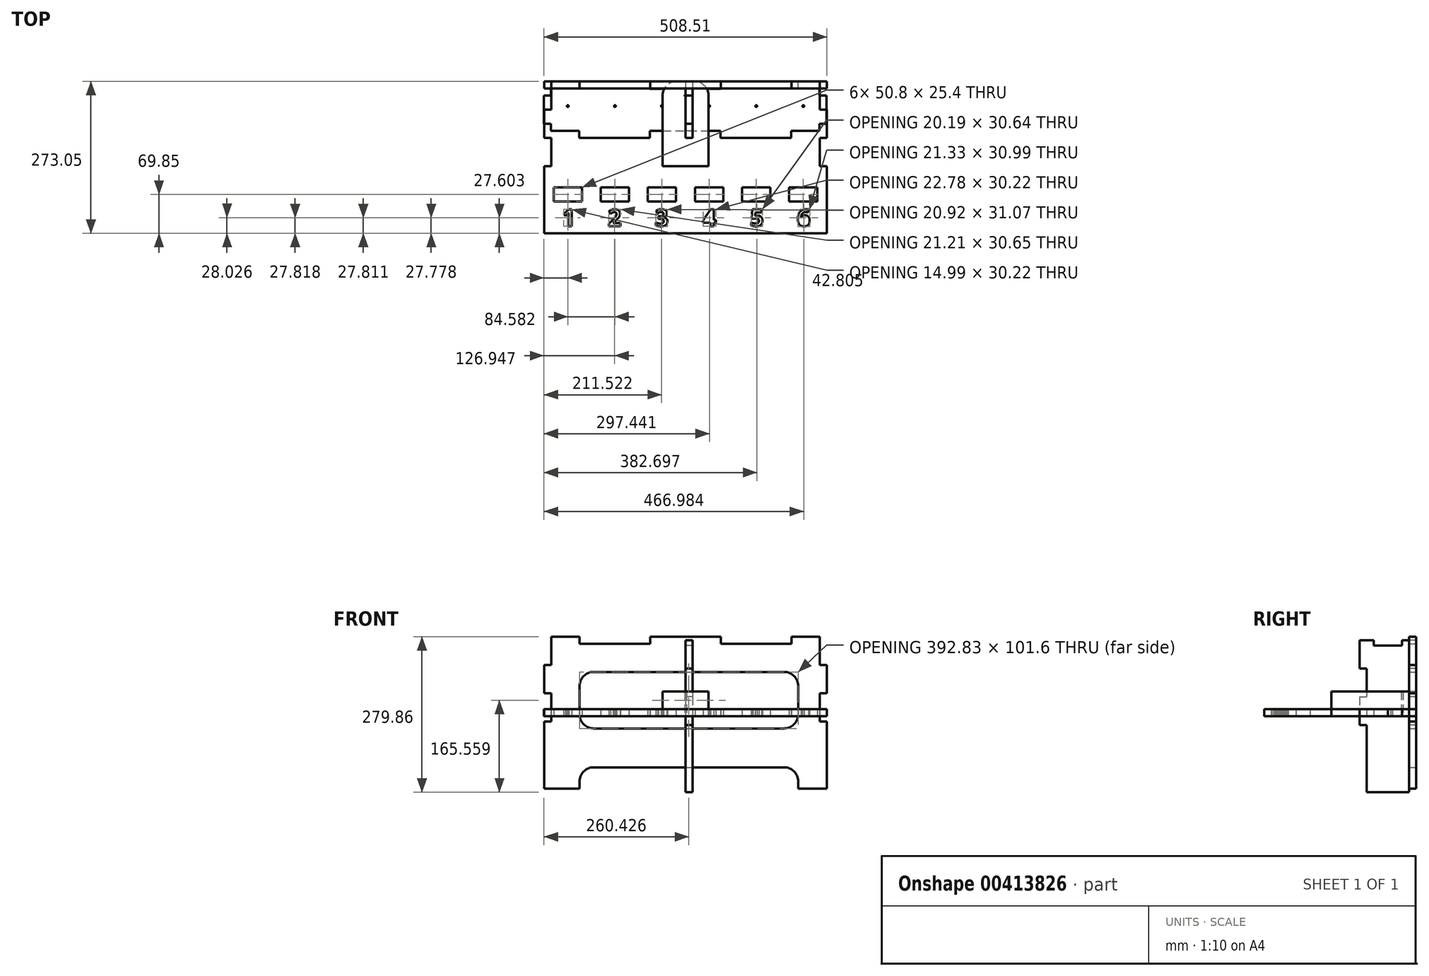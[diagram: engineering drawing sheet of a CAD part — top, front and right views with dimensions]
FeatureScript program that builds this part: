
annotation { "Feature Type Name" : "Feature", "Feature Type Description" : "" }
export const myFeature = defineFeature(function(context is Context, id is Id, definition is map)
    precondition{}
    {
        {
            var Q0;
            Q0=qCreatedBy(makeId("Top.planeOp"),FACE);
            var sketch = newSketch(context, id + "F0", { "sketchPlane" : qUnion([Q0])});
            skLineSegment(sketch, "E0.bottom", {"start": v(-15.88, 0) * mm, "end": v(15.88, 0) * mm});
            skLineSegment(sketch, "E0.top", {"start": v(-41.28, -152.4) * mm, "end": v(41.28, -152.4) * mm});
            skLineSegment(sketch, "E0.left", {"start": v(-41.28, -25.4) * mm, "end": v(-41.28, -152.4) * mm});
            skLineSegment(sketch, "E0.right", {"start": v(41.28, -25.4) * mm, "end": v(41.28, -152.4) * mm});
            skPoint(sketch, "E1.visualSharp", {"position": v(-41.28, 0) * mm});
            skArc(sketch, "E1.filletArc", {"start": v(-15.88, 0) * mm, "mid": v(-33.84, -7.44) * mm, "end": v(-41.28, -25.4) * mm});
            skPoint(sketch, "E2.visualSharp", {"position": v(41.28, 0) * mm});
            skArc(sketch, "E2.filletArc", {"start": v(41.28, -25.4) * mm, "mid": v(33.84, -7.44) * mm, "end": v(15.88, 0) * mm});
            skCircle(sketch, "E3", {"center": v(0, -25.4) * mm, "radius": 1.59 * mm});
            skSolve(sketch);
        }
        {
            var Q0;
            Q0 = qSketchRegion(id + "F0", true);
            extrude(context, id + "F1", {"entities" : qUnion([Q0]), "depth" : 44.45 * mm});
        }
        {
            var Q0;
            Q0=qCreatedBy(makeId("Top.planeOp"),FACE);
            var sketch = newSketch(context, id + "F2", { "sketchPlane" : qUnion([Q0])});
            skLineSegment(sketch, "E4.bottom", {"start": v(-241.3, 0) * mm, "end": v(-190.5, 0) * mm});
            skLineSegment(sketch, "E4.top", {"start": v(-254, -273.05) * mm, "end": v(254, -273.05) * mm});
            skLineSegment(sketch, "E4.left", {"start": v(-254, -50.8) * mm, "end": v(-254, -101.6) * mm});
            skLineSegment(sketch, "E4.right", {"start": v(254, -50.8) * mm, "end": v(254, -101.6) * mm});
            skLineSegment(sketch, "E5.bottom", {"start": v(-236.98, -190.5) * mm, "end": v(-186.18, -190.5) * mm});
            skLineSegment(sketch, "E5.top", {"start": v(-236.98, -215.9) * mm, "end": v(-186.18, -215.9) * mm});
            skLineSegment(sketch, "E5.left", {"start": v(-236.98, -190.5) * mm, "end": v(-236.98, -215.9) * mm});
            skLineSegment(sketch, "E5.right", {"start": v(-186.18, -190.5) * mm, "end": v(-186.18, -215.9) * mm});
            skLineSegment(sketch, "E6.bottom", {"start": v(-152.4, -190.5) * mm, "end": v(-101.6, -190.5) * mm});
            skLineSegment(sketch, "E6.top", {"start": v(-152.4, -215.9) * mm, "end": v(-101.6, -215.9) * mm});
            skLineSegment(sketch, "E6.left", {"start": v(-152.4, -190.5) * mm, "end": v(-152.4, -215.9) * mm});
            skLineSegment(sketch, "E6.right", {"start": v(-101.6, -190.5) * mm, "end": v(-101.6, -215.9) * mm});
            skLineSegment(sketch, "E7.bottom", {"start": v(-67.82, -190.5) * mm, "end": v(-17.02, -190.5) * mm});
            skLineSegment(sketch, "E7.top", {"start": v(-67.82, -215.9) * mm, "end": v(-17.02, -215.9) * mm});
            skLineSegment(sketch, "E7.left", {"start": v(-67.82, -190.5) * mm, "end": v(-67.82, -215.9) * mm});
            skLineSegment(sketch, "E7.right", {"start": v(-17.02, -190.5) * mm, "end": v(-17.02, -215.9) * mm});
            skLineSegment(sketch, "E8.bottom", {"start": v(236.98, -190.5) * mm, "end": v(186.18, -190.5) * mm});
            skLineSegment(sketch, "E8.top", {"start": v(236.98, -215.9) * mm, "end": v(186.18, -215.9) * mm});
            skLineSegment(sketch, "E8.left", {"start": v(236.98, -190.5) * mm, "end": v(236.98, -215.9) * mm});
            skLineSegment(sketch, "E8.right", {"start": v(186.18, -190.5) * mm, "end": v(186.18, -215.9) * mm});
            skLineSegment(sketch, "E9.bottom", {"start": v(152.4, -190.5) * mm, "end": v(101.6, -190.5) * mm});
            skLineSegment(sketch, "E9.top", {"start": v(152.4, -215.9) * mm, "end": v(101.6, -215.9) * mm});
            skLineSegment(sketch, "E9.left", {"start": v(152.4, -190.5) * mm, "end": v(152.4, -215.9) * mm});
            skLineSegment(sketch, "E9.right", {"start": v(101.6, -190.5) * mm, "end": v(101.6, -215.9) * mm});
            skLineSegment(sketch, "E10.bottom", {"start": v(67.82, -190.5) * mm, "end": v(17.02, -190.5) * mm});
            skLineSegment(sketch, "E10.top", {"start": v(67.82, -215.9) * mm, "end": v(17.02, -215.9) * mm});
            skLineSegment(sketch, "E10.left", {"start": v(67.82, -190.5) * mm, "end": v(67.82, -215.9) * mm});
            skLineSegment(sketch, "E10.right", {"start": v(17.02, -190.5) * mm, "end": v(17.02, -215.9) * mm});
            skText(sketch, "E11", { "text": "1", "fontName": "OpenSans-Bold.ttf"});
            skText(sketch, "E12", { "text": "2", "fontName": "OpenSans-Bold.ttf"});
            skText(sketch, "E13", { "text": "3", "fontName": "OpenSans-Bold.ttf"});
            skText(sketch, "E14", { "text": "4", "fontName": "OpenSans-Bold.ttf"});
            skText(sketch, "E15", { "text": "5", "fontName": "OpenSans-Bold.ttf"});
            skText(sketch, "E16", { "text": "6", "fontName": "OpenSans-Bold.ttf"});
            skCircle(sketch, "E17", {"center": v(-211.58, -44.45) * mm, "radius": 1.61 * mm});
            skCircle(sketch, "E18", {"center": v(-127, -44.45) * mm, "radius": 1.61 * mm});
            skCircle(sketch, "E19", {"center": v(-42.42, -44.45) * mm, "radius": 1.61 * mm});
            skCircle(sketch, "E20", {"center": v(211.58, -44.45) * mm, "radius": 1.61 * mm});
            skCircle(sketch, "E21", {"center": v(127, -44.45) * mm, "radius": 1.61 * mm});
            skCircle(sketch, "E22", {"center": v(42.42, -44.45) * mm, "radius": 1.61 * mm});
            skLineSegment(sketch, "E23.top", {"start": v(-254, -50.8) * mm, "end": v(-241.3, -50.8) * mm});
            skLineSegment(sketch, "E23.right", {"start": v(-241.3, 0) * mm, "end": v(-241.3, -50.8) * mm});
            skLineSegment(sketch, "E24.bottom", {"start": v(-254, -101.6) * mm, "end": v(-241.3, -101.6) * mm});
            skLineSegment(sketch, "E24.top", {"start": v(-254, -152.4) * mm, "end": v(-241.3, -152.4) * mm});
            skLineSegment(sketch, "E24.right", {"start": v(-241.3, -101.6) * mm, "end": v(-241.3, -152.4) * mm});
            skLineSegment(sketch, "E25.top", {"start": v(254, -50.8) * mm, "end": v(241.3, -50.8) * mm});
            skLineSegment(sketch, "E25.right", {"start": v(241.3, 0) * mm, "end": v(241.3, -50.8) * mm});
            skLineSegment(sketch, "E26.bottom", {"start": v(254, -101.6) * mm, "end": v(241.3, -101.6) * mm});
            skLineSegment(sketch, "E26.top", {"start": v(254, -152.4) * mm, "end": v(241.3, -152.4) * mm});
            skLineSegment(sketch, "E26.right", {"start": v(241.3, -101.6) * mm, "end": v(241.3, -152.4) * mm});
            skLineSegment(sketch, "E27.top", {"start": v(-190.5, -12.7) * mm, "end": v(-63.5, -12.7) * mm});
            skLineSegment(sketch, "E27.left", {"start": v(-190.5, 0) * mm, "end": v(-190.5, -12.7) * mm});
            skLineSegment(sketch, "E27.right", {"start": v(-63.5, 0) * mm, "end": v(-63.5, -12.7) * mm});
            skLineSegment(sketch, "E28.top", {"start": v(63.5, -12.7) * mm, "end": v(190.5, -12.7) * mm});
            skLineSegment(sketch, "E28.left", {"start": v(63.5, 0) * mm, "end": v(63.5, -12.7) * mm});
            skLineSegment(sketch, "E28.right", {"start": v(190.5, 0) * mm, "end": v(190.5, -12.7) * mm});
            skLineSegment(sketch, "E29.trimOffspring", {"start": v(-63.5, 0) * mm, "end": v(63.5, 0) * mm});
            skLineSegment(sketch, "E30.trimOffspring", {"start": v(190.5, 0) * mm, "end": v(241.3, 0) * mm});
            skPoint(sketch, "E31.orphan", {"position": v(254, 0) * mm});
            skLineSegment(sketch, "E32.trimOffspring", {"start": v(254, -152.4) * mm, "end": v(254, -273.05) * mm});
            skLineSegment(sketch, "E33.trimOffspring", {"start": v(-254, -152.4) * mm, "end": v(-254, -273.05) * mm});
            skPoint(sketch, "E23.bottom.start.orphan", {"position": v(-254, 0) * mm});
            skLineSegment(sketch, "E34.bottom", {"start": v(37.4, -249.16) * mm, "end": v(43.94, -249.16) * mm});
            skLineSegment(sketch, "E34.left", {"start": v(37.4, -249.16) * mm, "end": v(37.4, -254.07) * mm});
            skLineSegment(sketch, "E34.right", {"start": v(43.94, -249.16) * mm, "end": v(43.94, -254.07) * mm});
            const initialGuessF2  = {"E11": [-0.2217, -0.26035, 1, 0, 0.03048], "E12": [-0.13978, -0.26035, 1, 0, 0.03048], "E13": [-0.05506, -0.26035, 1, 0, 0.03048], "E14": [0.03082, -0.26035, 1, 0, 0.03048], "E15": [0.11602, -0.26035, 1, 0, 0.03048], "E16": [0.20032, -0.26035, 1, 0, 0.03048]};
            skSetInitialGuess(sketch, initialGuessF2);
            skSolve(sketch);
        }
        {
            var Q0;
            Q0 = qSketchRegion(id + "F2", true);
            extrude(context, id + "F3", {"entities" : qUnion([Q0]), "depth" : 12.7 * mm});
        }
        {
            var Q0;
            Q0=qCreatedBy(makeId("Front.planeOp"),FACE);
            var sketch = newSketch(context, id + "F4", { "sketchPlane" : qUnion([Q0])});
            skLineSegment(sketch, "E35.bottom", {"start": v(-241.3, 143.33) * mm, "end": v(-190.5, 143.33) * mm});
            skLineSegment(sketch, "E35.top", {"start": v(-254, -129.72) * mm, "end": v(-190.5, -129.72) * mm});
            skLineSegment(sketch, "E35.left", {"start": v(-254, 92.53) * mm, "end": v(-254, 41.73) * mm});
            skLineSegment(sketch, "E35.right", {"start": v(254, 92.53) * mm, "end": v(254, 41.73) * mm});
            skLineSegment(sketch, "E36.top", {"start": v(-254, 92.53) * mm, "end": v(-241.3, 92.53) * mm});
            skLineSegment(sketch, "E36.right", {"start": v(-241.3, 143.33) * mm, "end": v(-241.3, 92.53) * mm});
            skLineSegment(sketch, "E37.bottom", {"start": v(-254, 41.73) * mm, "end": v(-241.3, 41.73) * mm});
            skLineSegment(sketch, "E37.top", {"start": v(-254, -9.07) * mm, "end": v(-241.3, -9.07) * mm});
            skLineSegment(sketch, "E37.right", {"start": v(-241.3, 41.73) * mm, "end": v(-241.3, -9.07) * mm});
            skLineSegment(sketch, "E38.top", {"start": v(254, 92.53) * mm, "end": v(241.3, 92.53) * mm});
            skLineSegment(sketch, "E38.right", {"start": v(241.3, 143.33) * mm, "end": v(241.3, 92.53) * mm});
            skLineSegment(sketch, "E39.bottom", {"start": v(254, 41.73) * mm, "end": v(241.3, 41.73) * mm});
            skLineSegment(sketch, "E39.top", {"start": v(254, -9.07) * mm, "end": v(241.3, -9.07) * mm});
            skLineSegment(sketch, "E39.right", {"start": v(241.3, 41.73) * mm, "end": v(241.3, -9.07) * mm});
            skLineSegment(sketch, "E40.top", {"start": v(-190.5, 130.63) * mm, "end": v(-63.5, 130.63) * mm});
            skLineSegment(sketch, "E40.left", {"start": v(-190.5, 143.33) * mm, "end": v(-190.5, 130.63) * mm});
            skLineSegment(sketch, "E40.right", {"start": v(-63.5, 143.33) * mm, "end": v(-63.5, 130.63) * mm});
            skLineSegment(sketch, "E41.top", {"start": v(63.5, 130.63) * mm, "end": v(190.5, 130.63) * mm});
            skLineSegment(sketch, "E41.left", {"start": v(63.5, 143.33) * mm, "end": v(63.5, 130.63) * mm});
            skLineSegment(sketch, "E41.right", {"start": v(190.5, 143.33) * mm, "end": v(190.5, 130.63) * mm});
            skLineSegment(sketch, "E42.trimOffspring", {"start": v(-63.5, 143.33) * mm, "end": v(63.5, 143.33) * mm});
            skLineSegment(sketch, "E43.trimOffspring", {"start": v(190.5, 143.33) * mm, "end": v(241.3, 143.33) * mm});
            skPoint(sketch, "E44.orphan", {"position": v(254, 143.33) * mm});
            skLineSegment(sketch, "E45.trimOffspring", {"start": v(254, -9.07) * mm, "end": v(254, -129.72) * mm});
            skLineSegment(sketch, "E46.trimOffspring", {"start": v(-254, -9.07) * mm, "end": v(-254, -129.72) * mm});
            skPoint(sketch, "E36.bottom.start.orphan", {"position": v(-254, 143.33) * mm});
            skLineSegment(sketch, "E47.bottom", {"start": v(-165.1, 79.83) * mm, "end": v(176.93, 79.83) * mm});
            skLineSegment(sketch, "E47.top", {"start": v(-165.1, -21.77) * mm, "end": v(176.93, -21.77) * mm});
            skLineSegment(sketch, "E47.left", {"start": v(-190.5, 54.43) * mm, "end": v(-190.5, 3.63) * mm});
            skLineSegment(sketch, "E47.right", {"start": v(202.33, 54.43) * mm, "end": v(202.33, 3.63) * mm});
            skPoint(sketch, "E48.visualSharp", {"position": v(-190.5, 79.83) * mm});
            skArc(sketch, "E48.filletArc", {"start": v(-165.1, 79.83) * mm, "mid": v(-183.06, 72.39) * mm, "end": v(-190.5, 54.43) * mm});
            skPoint(sketch, "E49.visualSharp", {"position": v(202.33, 79.83) * mm});
            skArc(sketch, "E49.filletArc", {"start": v(202.33, 54.43) * mm, "mid": v(194.9, 72.39) * mm, "end": v(176.93, 79.83) * mm});
            skPoint(sketch, "E50.visualSharp", {"position": v(202.33, -21.77) * mm});
            skArc(sketch, "E50.filletArc", {"start": v(176.93, -21.77) * mm, "mid": v(194.9, -14.33) * mm, "end": v(202.33, 3.63) * mm});
            skPoint(sketch, "E51.visualSharp", {"position": v(-190.5, -21.77) * mm});
            skArc(sketch, "E51.filletArc", {"start": v(-190.5, 3.63) * mm, "mid": v(-183.06, -14.33) * mm, "end": v(-165.1, -21.77) * mm});
            skLineSegment(sketch, "E52.top", {"start": v(-165.1, -91.62) * mm, "end": v(176.93, -91.62) * mm});
            skLineSegment(sketch, "E52.left", {"start": v(-190.5, -129.72) * mm, "end": v(-190.5, -117.02) * mm});
            skLineSegment(sketch, "E52.right", {"start": v(202.33, -129.72) * mm, "end": v(202.33, -117.02) * mm});
            skPoint(sketch, "E53.visualSharp", {"position": v(-190.5, -91.62) * mm});
            skArc(sketch, "E53.filletArc", {"start": v(-165.1, -91.62) * mm, "mid": v(-183.06, -99.06) * mm, "end": v(-190.5, -117.02) * mm});
            skPoint(sketch, "E54.visualSharp", {"position": v(202.33, -91.62) * mm});
            skArc(sketch, "E54.filletArc", {"start": v(202.33, -117.02) * mm, "mid": v(194.9, -99.06) * mm, "end": v(176.93, -91.62) * mm});
            skLineSegment(sketch, "E55.trimOffspring", {"start": v(202.33, -129.72) * mm, "end": v(254, -129.72) * mm});
            skSolve(sketch);
        }
        {
            var Q0;
            Q0 = qSketchRegion(id + "F4", true);
            extrude(context, id + "F5", {"entities" : qUnion([Q0]), "depth" : 12.7 * mm});
        }
        {
            var Q0;
            Q0=qCreatedBy(makeId("Right.planeOp"),FACE);
            var sketch = newSketch(context, id + "F6", { "sketchPlane" : qUnion([Q0])});
            skLineSegment(sketch, "E56.bottom", {"start": v(0, 136.53) * mm, "end": v(-25.4, 136.53) * mm});
            skLineSegment(sketch, "E56.top", {"start": v(-12.7, -136.53) * mm, "end": v(-88.9, -136.53) * mm});
            skLineSegment(sketch, "E56.left", {"start": v(0, 136.53) * mm, "end": v(0, 85.72) * mm});
            skLineSegment(sketch, "E56.right", {"start": v(-101.6, 136.53) * mm, "end": v(-101.6, 85.72) * mm});
            skLineSegment(sketch, "E57.bottom", {"start": v(0, 85.72) * mm, "end": v(-12.7, 85.72) * mm});
            skLineSegment(sketch, "E57.top", {"start": v(0, 34.92) * mm, "end": v(-12.7, 34.92) * mm});
            skLineSegment(sketch, "E57.right", {"start": v(-12.7, 85.72) * mm, "end": v(-12.7, 34.92) * mm});
            skLineSegment(sketch, "E58.bottom", {"start": v(0, -15.88) * mm, "end": v(-12.7, -15.88) * mm});
            skLineSegment(sketch, "E58.right", {"start": v(-12.7, -15.88) * mm, "end": v(-12.7, -136.53) * mm});
            skLineSegment(sketch, "E59.top", {"start": v(-25.4, 127.39) * mm, "end": v(-76.2, 127.39) * mm});
            skLineSegment(sketch, "E59.left", {"start": v(-25.4, 136.53) * mm, "end": v(-25.4, 127.39) * mm});
            skLineSegment(sketch, "E59.right", {"start": v(-76.2, 136.53) * mm, "end": v(-76.2, 127.39) * mm});
            skLineSegment(sketch, "E60.trimOffspring", {"start": v(-76.2, 136.53) * mm, "end": v(-101.6, 136.53) * mm});
            skLineSegment(sketch, "E61.bottom", {"start": v(-101.6, 85.72) * mm, "end": v(-88.9, 85.72) * mm});
            skLineSegment(sketch, "E61.top", {"start": v(-101.6, 34.92) * mm, "end": v(-88.9, 34.92) * mm});
            skLineSegment(sketch, "E61.right", {"start": v(-88.9, 85.72) * mm, "end": v(-88.9, 34.92) * mm});
            skLineSegment(sketch, "E62.bottom", {"start": v(-101.6, -15.88) * mm, "end": v(-88.9, -15.88) * mm});
            skLineSegment(sketch, "E62.right", {"start": v(-88.9, -15.88) * mm, "end": v(-88.9, -136.53) * mm});
            skLineSegment(sketch, "E63.trimOffspring", {"start": v(-101.6, 34.92) * mm, "end": v(-101.6, -15.88) * mm});
            skPoint(sketch, "E64.orphan", {"position": v(0, -136.53) * mm});
            skLineSegment(sketch, "E65.trimOffspring", {"start": v(0, 34.92) * mm, "end": v(0, -15.88) * mm});
            skSolve(sketch);
        }
        {
            var Q0;
            Q0 = qSketchRegion(id + "F6", true);
            extrude(context, id + "F7", {"entities" : qUnion([Q0]), "depth" : 12.7 * mm});
        }
        {
            var Q0;
            Q0=qCreatedBy(makeId("Top.planeOp"),FACE);
            var sketch = newSketch(context, id + "F8", { "sketchPlane" : qUnion([Q0])});
            skLineSegment(sketch, "E66.left", {"start": v(-254.5, -25.4) * mm, "end": v(-254.5, -76.2) * mm});
            skLineSegment(sketch, "E67.top", {"start": v(-254.5, -25.4) * mm, "end": v(-241.8, -25.4) * mm});
            skLineSegment(sketch, "E67.right", {"start": v(-241.8, -12.7) * mm, "end": v(-241.8, -25.4) * mm});
            skLineSegment(sketch, "E68.top", {"start": v(-254.5, -76.2) * mm, "end": v(-241.8, -76.2) * mm});
            skLineSegment(sketch, "E68.right", {"start": v(-241.8, -88.9) * mm, "end": v(-241.8, -76.2) * mm});
            skLineSegment(sketch, "E69.top", {"start": v(253.5, -25.4) * mm, "end": v(240.8, -25.4) * mm});
            skLineSegment(sketch, "E69.right", {"start": v(240.8, -11.99) * mm, "end": v(240.8, -25.4) * mm});
            skLineSegment(sketch, "E70.top", {"start": v(253.5, -76.2) * mm, "end": v(240.8, -76.2) * mm});
            skLineSegment(sketch, "E70.right", {"start": v(240.8, -88.9) * mm, "end": v(240.8, -76.2) * mm});
            skPoint(sketch, "E71.oppositeSnap0", {"position": v(-241.8, -12.7) * mm});
            skLineSegment(sketch, "E71.top", {"start": v(-241.8, -12.7) * mm, "end": v(-191, -12.7) * mm});
            skLineSegment(sketch, "E71.right", {"start": v(-191, 0) * mm, "end": v(-191, -12.7) * mm});
            skLineSegment(sketch, "E72.top", {"start": v(-64, -13.57) * mm, "end": v(63, -13.57) * mm});
            skLineSegment(sketch, "E72.left", {"start": v(-64, 0) * mm, "end": v(-64, -13.57) * mm});
            skLineSegment(sketch, "E72.right", {"start": v(63, 0) * mm, "end": v(63, -13.57) * mm});
            skLineSegment(sketch, "E73.top", {"start": v(240.8, -11.99) * mm, "end": v(190, -11.99) * mm});
            skLineSegment(sketch, "E73.right", {"start": v(190, 0) * mm, "end": v(190, -11.99) * mm});
            skLineSegment(sketch, "E74.top", {"start": v(-64, -88.9) * mm, "end": v(63, -88.9) * mm});
            skLineSegment(sketch, "E74.left", {"start": v(-64, -101.6) * mm, "end": v(-64, -88.9) * mm});
            skLineSegment(sketch, "E74.right", {"start": v(63, -101.6) * mm, "end": v(63, -88.9) * mm});
            skLineSegment(sketch, "E75.top", {"start": v(190, -88.9) * mm, "end": v(240.8, -88.9) * mm});
            skLineSegment(sketch, "E75.left", {"start": v(190, -101.6) * mm, "end": v(190, -88.9) * mm});
            skLineSegment(sketch, "E76.top", {"start": v(-191, -88.9) * mm, "end": v(-241.8, -88.9) * mm});
            skLineSegment(sketch, "E76.left", {"start": v(-191, -101.6) * mm, "end": v(-191, -88.9) * mm});
            skLineSegment(sketch, "E77.trimOffspring", {"start": v(63, 0) * mm, "end": v(190, 0) * mm});
            skLineSegment(sketch, "E78.trimOffspring", {"start": v(-191, 0) * mm, "end": v(-64, 0) * mm});
            skPoint(sketch, "E67.bottom.start.orphan", {"position": v(-254.5, 0) * mm});
            skPoint(sketch, "E79.orphan", {"position": v(-241.8, 0) * mm});
            skLineSegment(sketch, "E80.trimOffspring", {"start": v(63, -101.6) * mm, "end": v(190, -101.6) * mm});
            skLineSegment(sketch, "E81.trimOffspring", {"start": v(-191, -101.6) * mm, "end": v(-64, -101.6) * mm});
            skPoint(sketch, "E82.orphan", {"position": v(-254.5, -88.9) * mm});
            skPoint(sketch, "E83.orphan", {"position": v(-254.5, -101.6) * mm});
            skPoint(sketch, "E84.orphan", {"position": v(253.5, -101.6) * mm});
            skPoint(sketch, "E70.left.start.orphan", {"position": v(253.5, -88.9) * mm});
            skLineSegment(sketch, "E85.trimOffspring", {"start": v(253.5, -25.4) * mm, "end": v(253.5, -76.2) * mm});
            skPoint(sketch, "E69.bottom.start.orphan", {"position": v(253.5, 0) * mm});
            skPoint(sketch, "E86.orphan", {"position": v(240.8, 0) * mm});
            skSolve(sketch);
        }
        {
            var Q0;
            Q0 = qSketchRegion(id + "F8", true);
            extrude(context, id + "F9", {"entities" : qUnion([Q0]), "depth" : 12.7 * mm});
        }
    });
